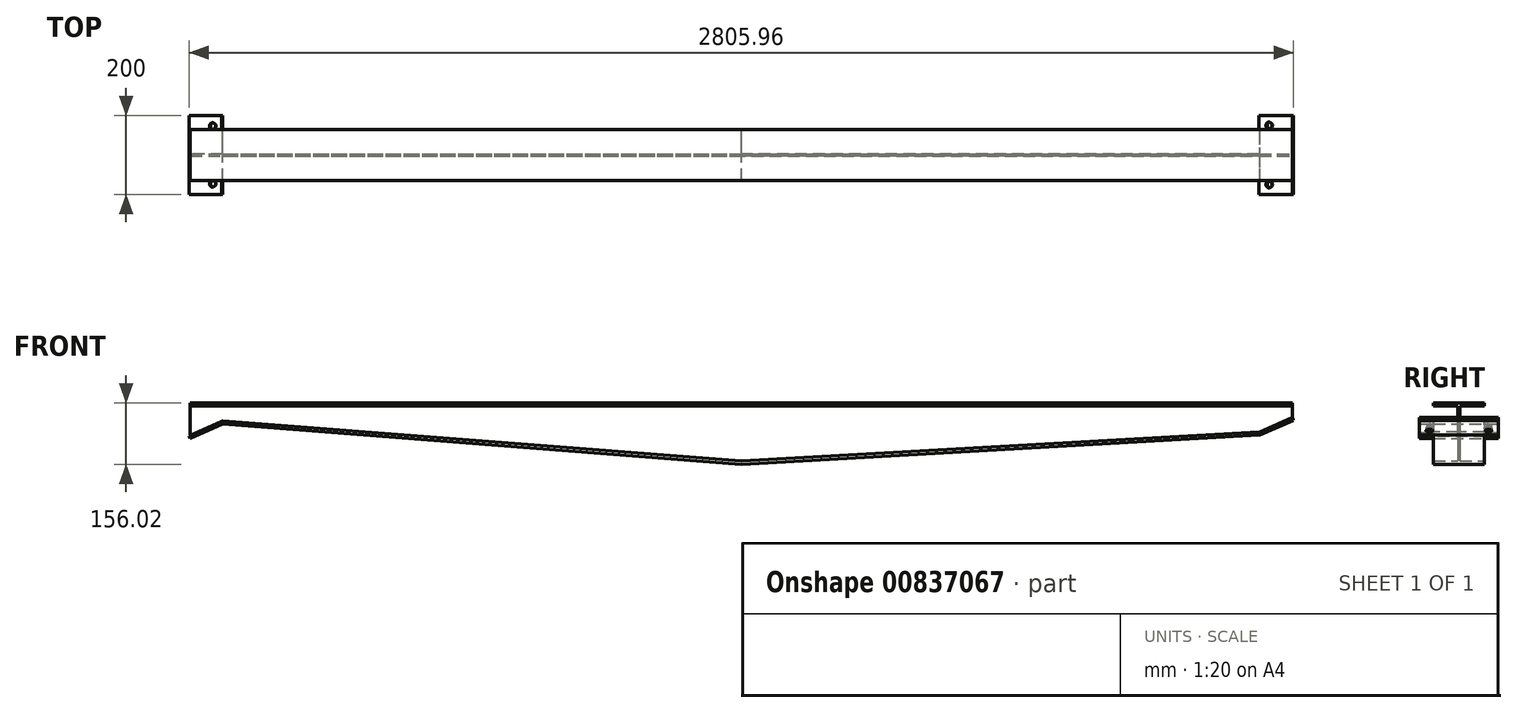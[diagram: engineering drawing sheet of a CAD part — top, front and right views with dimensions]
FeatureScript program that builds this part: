
annotation { "Feature Type Name" : "Feature", "Feature Type Description" : "" }
export const myFeature = defineFeature(function(context is Context, id is Id, definition is map)
    precondition{}
    {
        {
            var Q0;
            Q0=qCreatedBy(makeId("Front.planeOp"),FACE);
            var sketch = newSketch(context, id + "F0", { "sketchPlane" : qUnion([Q0])});
            skLineSegment(sketch, "E0", {"start": v(0, 140) * mm, "end": v(-1400, 140) * mm});
            skLineSegment(sketch, "E1.MirrorCS", {"start": v(0, 140) * mm, "end": v(1400, 140) * mm});
            skLineSegment(sketch, "E2", {"start": v(1400, 140) * mm, "end": v(1400, 110.6) * mm});
            skLineSegment(sketch, "E3", {"start": v(1400, 110.6) * mm, "end": v(1317.78, 74) * mm});
            skLineSegment(sketch, "E4", {"start": v(1317.78, 74) * mm, "end": v(0, 0) * mm});
            skLineSegment(sketch, "E5", {"start": v(-1400, 65.4) * mm, "end": v(-1317.78, 102) * mm});
            skLineSegment(sketch, "E6", {"start": v(-1400, 65.4) * mm, "end": v(-1400, 140) * mm});
            skLineSegment(sketch, "E7", {"start": v(-1317.78, 102) * mm, "end": v(0, 0) * mm});
            skSolve(sketch);
        }
        {
            var Q0;
            Q0=qSketchRegion(id+"F0",true);
            extrude(context, id + "F1", {"entities" : qUnion([Q0]), "depth" : 5 * mm, "offsetDistance" : 25 * mm, "symmetric" : true});
        }
        {
            var Q0;
            Q0=qCreatedBy(makeId("Front.planeOp"),FACE);
            var sketch = newSketch(context, id + "F2", { "sketchPlane" : qUnion([Q0])});
            skLineSegment(sketch, "E8", {"start": v(0, 0) * mm, "end": v(-1317.78, 102) * mm});
            skLineSegment(sketch, "E9", {"start": v(-1317.78, 93.98) * mm, "end": v(0, -8.02) * mm});
            skLineSegment(sketch, "E10", {"start": v(0, 140) * mm, "end": v(-1400, 140) * mm});
            skLineSegment(sketch, "E11", {"start": v(-1400, 140) * mm, "end": v(-1400, 148) * mm});
            skLineSegment(sketch, "E12", {"start": v(-1400, 148) * mm, "end": v(0, 148) * mm});
            skLineSegment(sketch, "E13.MirrorCS", {"start": v(0, 140) * mm, "end": v(1400, 140) * mm});
            skLineSegment(sketch, "E14.MirrorCS", {"start": v(1400, 148) * mm, "end": v(0, 148) * mm});
            skLineSegment(sketch, "E15.MirrorCS", {"start": v(1400, 140) * mm, "end": v(1400, 148) * mm});
            skLineSegment(sketch, "E16", {"start": v(1400, 110.6) * mm, "end": v(1317.78, 74) * mm});
            skLineSegment(sketch, "E17", {"start": v(1317.78, 74) * mm, "end": v(0, 0) * mm});
            skLineSegment(sketch, "E18", {"start": v(1400, 110.6) * mm, "end": v(1400, 102.58) * mm});
            skLineSegment(sketch, "E19", {"start": v(1400, 102.58) * mm, "end": v(1317.78, 65.98) * mm});
            skLineSegment(sketch, "E20", {"start": v(1317.78, 65.98) * mm, "end": v(0, -8.02) * mm});
            skLineSegment(sketch, "E21", {"start": v(-1317.78, 102) * mm, "end": v(-1400, 65.4) * mm});
            skLineSegment(sketch, "E22", {"start": v(-1400, 65.4) * mm, "end": v(-1400, 57.37) * mm});
            skLineSegment(sketch, "E23", {"start": v(-1400, 57.37) * mm, "end": v(-1317.78, 93.98) * mm});
            skSolve(sketch);
        }
        {
            var Q0;
            Q0=qSketchRegion(id+"F2",true);
            extrude(context, id + "F3", {"entities" : qUnion([Q0]), "operationType" : NewBodyOperationType.ADD, "depth" : 130 * mm, "offsetDistance" : 25 * mm, "symmetric" : true});
        }
        {
            var Q0;
            Q0=qCreatedBy(makeId("Front.planeOp"),FACE);
            var sketch = newSketch(context, id + "F4", { "sketchPlane" : qUnion([Q0])});
            skLineSegment(sketch, "E24", {"start": v(0, 0) * mm, "end": v(0, -96.56) * mm, "construction": true});
            skLineSegment(sketch, "E25", {"start": v(0, -96.56) * mm, "end": v(-31.38, 0) * mm, "construction": true});
            skSolve(sketch);
        }
        {
            var Q0;
            Q0=makeQuery(id+"F3.opExtrude","SWEPT_FACE",FACE,{"disambiguationData":[OSD([sQuery(id+"F2.wireOp",EDGE,"E19")])]});
            var sketch = newSketch(context, id + "F5", { "sketchPlane" : qUnion([Q0])});
            skLineSegment(sketch, "E26.bottom", {"start": v(1323.95, 100) * mm, "end": v(1230.69, 100) * mm});
            skLineSegment(sketch, "E26.top", {"start": v(1323.95, -100) * mm, "end": v(1230.69, -100) * mm});
            skLineSegment(sketch, "E26.left", {"start": v(1323.95, 100) * mm, "end": v(1323.95, -100) * mm});
            skLineSegment(sketch, "E26.right", {"start": v(1230.69, 100) * mm, "end": v(1230.69, -100) * mm});
            skLineSegment(sketch, "E27", {"start": v(1323.95, 0) * mm, "end": v(1230.69, 0) * mm, "construction": true});
            skCircle(sketch, "E28", {"center": v(1258.95, 75) * mm, "radius": 8.5 * mm});
            skCircle(sketch, "E29.MirrorC", {"center": v(1258.95, -75) * mm, "radius": 8.5 * mm});
            skSolve(sketch);
        }
        {
            var Q0;
            Q0 = qSketchRegion(id + "F5", true);
            extrude(context, id + "F6", {"entities" : qUnion([Q0]), "operationType" : NewBodyOperationType.ADD, "oppositeDirection" : true, "depth" : 8 * mm, "offsetDistance" : 25 * mm});
        }
        {
            var Q0;
            Q0=makeQuery(id+"F3.opExtrude","SWEPT_FACE",FACE,{"disambiguationData":[OSD([sQuery(id+"F2.wireOp",EDGE,"E23")])]});
            var sketch = newSketch(context, id + "F7", { "sketchPlane" : qUnion([Q0])});
            skLineSegment(sketch, "E30.bottom", {"start": v(-1255.63, 100) * mm, "end": v(-1165.63, 100) * mm});
            skLineSegment(sketch, "E30.top", {"start": v(-1255.63, -100) * mm, "end": v(-1165.63, -100) * mm});
            skLineSegment(sketch, "E30.left", {"start": v(-1255.63, 100) * mm, "end": v(-1255.63, -100) * mm});
            skLineSegment(sketch, "E30.right", {"start": v(-1165.63, 100) * mm, "end": v(-1165.63, -100) * mm});
            skLineSegment(sketch, "E31", {"start": v(-1255.63, 0) * mm, "end": v(-1165.63, 0) * mm, "construction": true});
            skCircle(sketch, "E32", {"center": v(-1190.63, -73.4) * mm, "radius": 8.5 * mm});
            skCircle(sketch, "E33.MirrorC", {"center": v(-1190.63, 73.4) * mm, "radius": 8.5 * mm});
            skSolve(sketch);
        }
        {
            var Q0;
            Q0 = qSketchRegion(id + "F7", true);
            extrude(context, id + "F8", {"entities" : qUnion([Q0]), "operationType" : NewBodyOperationType.ADD, "oppositeDirection" : true, "depth" : 7.33 * mm, "offsetDistance" : 25 * mm});
        }
    });
